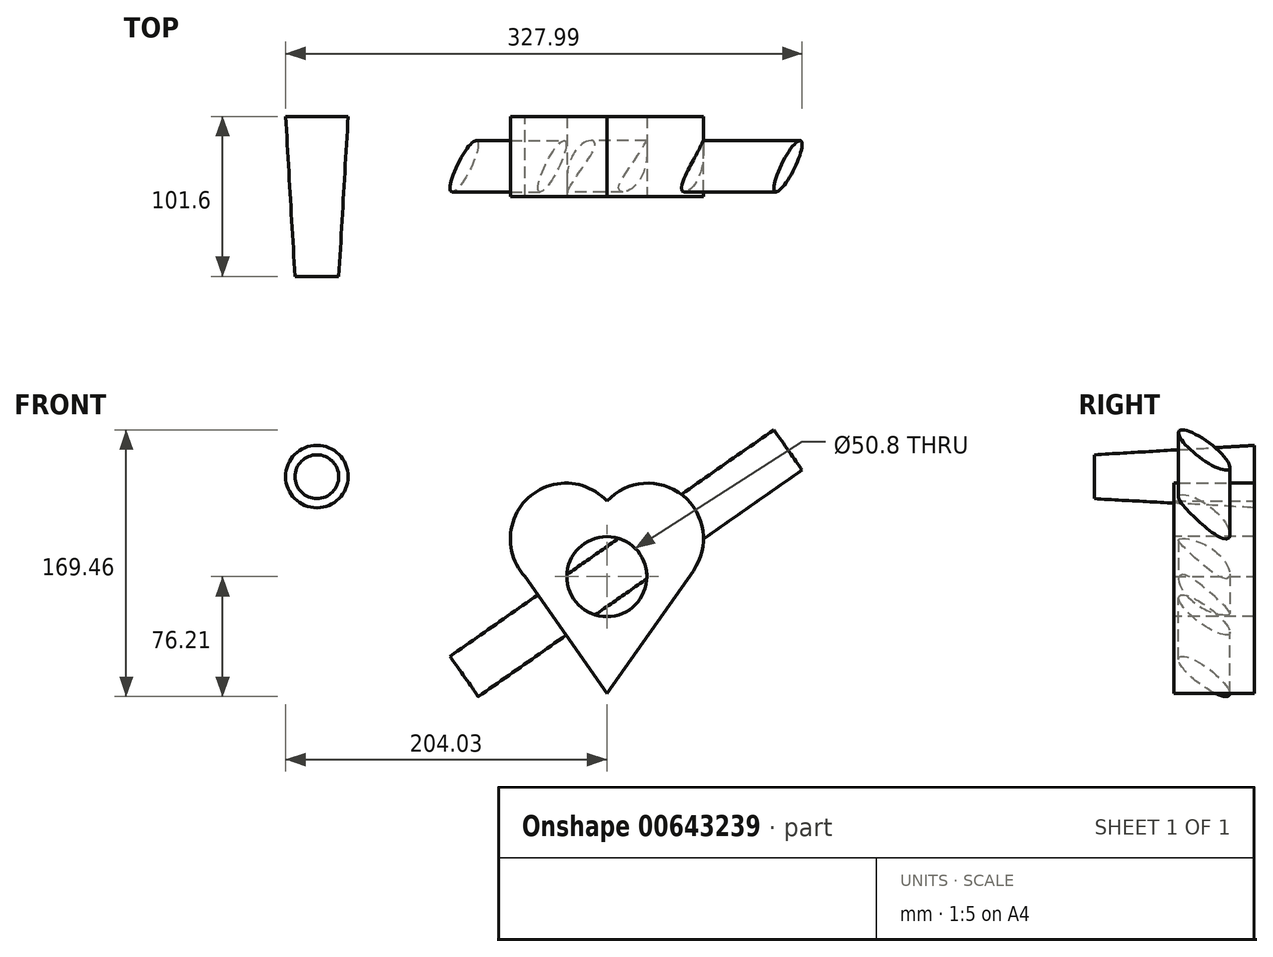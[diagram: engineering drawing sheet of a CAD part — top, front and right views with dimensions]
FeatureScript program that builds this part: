
annotation { "Feature Type Name" : "Feature", "Feature Type Description" : "" }
export const myFeature = defineFeature(function(context is Context, id is Id, definition is map)
    precondition{}
    {
        {
            var Q0;
            Q0=qCreatedBy(makeId("Front.planeOp"),FACE);
            var sketch = newSketch(context, id + "F0", { "sketchPlane" : qUnion([Q0])});
            skArc(sketch, "E0", {"start": v(-0.02, 47.95) * mm, "mid": v(-50, 49.99) * mm, "end": v(-51.91, 0) * mm});
            skArc(sketch, "E1", {"start": v(54.88, 3.7) * mm, "mid": v(48.17, 51.54) * mm, "end": v(-0.02, 47.95) * mm});
            skLineSegment(sketch, "E2", {"start": v(-51.91, 0) * mm, "end": v(0, -74.22) * mm});
            skLineSegment(sketch, "E3", {"start": v(0, -74.22) * mm, "end": v(54.88, 3.7) * mm});
            skPoint(sketch, "E4.orphan", {"position": v(52.27, 0) * mm});
            skSolve(sketch);
        }
        {
            var Q0;
            Q0=makeQuery(id+"F0.imprint","IMPRINT",FACE,{"disambiguationData":[TD([[makeQuery(id+"F0.imprint","IMPRINT",EDGE,{"derivedFrom":sQuery(id+"F0.wireOp",EDGE,"E0")}),1.0]])]});
            extrude(context, id + "F1", {"entities" : qUnion([Q0]), "depth" : 50.8 * mm, "offsetDistance" : 25.4 * mm});
        }
        {
            var Q0;
            Q0=makeQuery(id+"F1.opExtrude","CAP_FACE",FACE,{"disambiguationData":[OSD([sQuery(id+"F0.wireOp",EDGE,"E0"),sQuery(id+"F0.wireOp",EDGE,"E1"),sQuery(id+"F0.wireOp",EDGE,"E2"),sQuery(id+"F0.wireOp",EDGE,"E3")])],"isStart":false});
            var sketch = newSketch(context, id + "F2", { "sketchPlane" : qUnion([Q0])});
            skCircle(sketch, "E5", {"center": v(0, 0) * mm, "radius": 19.46 * mm});
            skSolve(sketch);
        }
        {
            var Q0;
            Q0=sQuery(id+"F2.wireOp",VERTEX,"E5.center");
            var Q1;
            Q1=makeQuery(id+"F1.opExtrude","SWEPT_BODY",BODY,{"disambiguationData":[OSD([sQuery(id+"F0.wireOp",EDGE,"E0"),sQuery(id+"F0.wireOp",EDGE,"E1"),sQuery(id+"F0.wireOp",EDGE,"E2"),sQuery(id+"F0.wireOp",EDGE,"E3")])]});
            hole(context, id + "F3", {"style" : HoleStyle.SIMPLE, "endStyle" : HoleEndStyle.THROUGH, "holeDiameter" : 50.8 * mm, "majorDiameter" : 6.35 * mm, "isTappedThrough" : true, "tappedDepth" : 12.7 * mm, "tapClearance" : 3, "locations" : qUnion([Q0]), "scope" : qUnion([Q1])});
        }
        {
            var Q0;
            Q0=makeQuery(id+"F1.opExtrude","SWEPT_FACE",FACE,{"disambiguationData":[OSD([sQuery(id+"F0.wireOp",EDGE,"E2")])]});
            var sketch = newSketch(context, id + "F4", { "sketchPlane" : qUnion([Q0])});
            skEllipse(sketch, "E6", {"center": v(31.7, 0) * mm, "majorRadius": 21.75 * mm, "minorRadius": 6.23 * mm, "majorAxis": v(-0.73, -0.69)});
            skSolve(sketch);
        }
        {
            var Q0;
            Q0 = qSketchRegion(id + "F4", true);
            extrude(context, id + "F5", {"entities" : qUnion([Q0]), "operationType" : NewBodyOperationType.ADD, "oppositeDirection" : true, "depth" : 182.88 * mm, "offsetDistance" : 25.4 * mm, "hasSecondDirection" : true, "secondDirectionOppositeDirection" : false, "secondDirectionDepth" : 68.07 * mm});
        }
        {
            var Q0;
            Q0=qCreatedBy(makeId("Front.planeOp"),FACE);
            var sketch = newSketch(context, id + "F6", { "sketchPlane" : qUnion([Q0])});
            skCircle(sketch, "E7", {"center": v(-184.2, 63.53) * mm, "radius": 19.84 * mm});
            skSolve(sketch);
        }
        {
            var Q0;
            Q0=qCreatedBy(makeId("Front.planeOp"),FACE);
            cPlane(context, id + "F7", {"entities" : qUnion([Q0]), "cplaneType" : CPlaneType.OFFSET, "offset" : 101.6 * mm, "width" : 152.4 * mm, "height" : 152.4 * mm});
        }
        {
            var Q0;
            Q0=qCreatedBy(id+"F7.planeOp",FACE);
            var sketch = newSketch(context, id + "F8", { "sketchPlane" : qUnion([Q0])});
            skCircle(sketch, "E8", {"center": v(-184.22, 63.45) * mm, "radius": 13.93 * mm});
            skSolve(sketch);
        }
        {
            var Q0;
            Q0=makeQuery(id+"F6.imprint","IMPRINT",FACE,{"disambiguationData":[TD([[makeQuery(id+"F6.imprint","IMPRINT",EDGE,{"derivedFrom":sQuery(id+"F6.wireOp",EDGE,"E7")}),1.0]])]});
            var Q1;
            Q1=makeQuery(id+"F8.imprint","IMPRINT",FACE,{"disambiguationData":[TD([[makeQuery(id+"F8.imprint","IMPRINT",EDGE,{"derivedFrom":sQuery(id+"F8.wireOp",EDGE,"E8")}),1.0]])]});
            loft(context, id + "F9", {"sheetProfilesArray" : [{ "sheetProfileEntities" : qUnion([Q0]) }, { "sheetProfileEntities" : qUnion([Q1]) }]});
        }
    });
